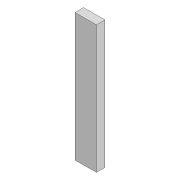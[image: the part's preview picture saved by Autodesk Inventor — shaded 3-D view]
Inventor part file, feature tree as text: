
AUTODESK INVENTOR PART (.ipt)
format: ipt  version: 2021 (Build 250183000, 183)  size: 107,008 bytes
history: native  units: in
note: dims shown in document units (in); Inventor stores cm internally (conversion verified against a paired STEP export)
features: extrude x1, sketch x1
ambient origin geometry x8: Origin, YZ Plane, XZ Plane, XY Plane, X Axis, Y Axis, Z Axis, Center Point
bodies: Body1 (feature_tree)
feature tree (2):
  extrude  "Extrusion2"  Depth=118.1102in TaperAngle=360.0deg
  sketch  "Sketch1"  dims[d0=118.1102in d1=6.2992in d3=360.0deg d7=1968.5039in d8=1.5748in d10=360.0deg d12=3.0in d14=7.874in d15=19.685in d16=118.1102in d17=0.0in]
